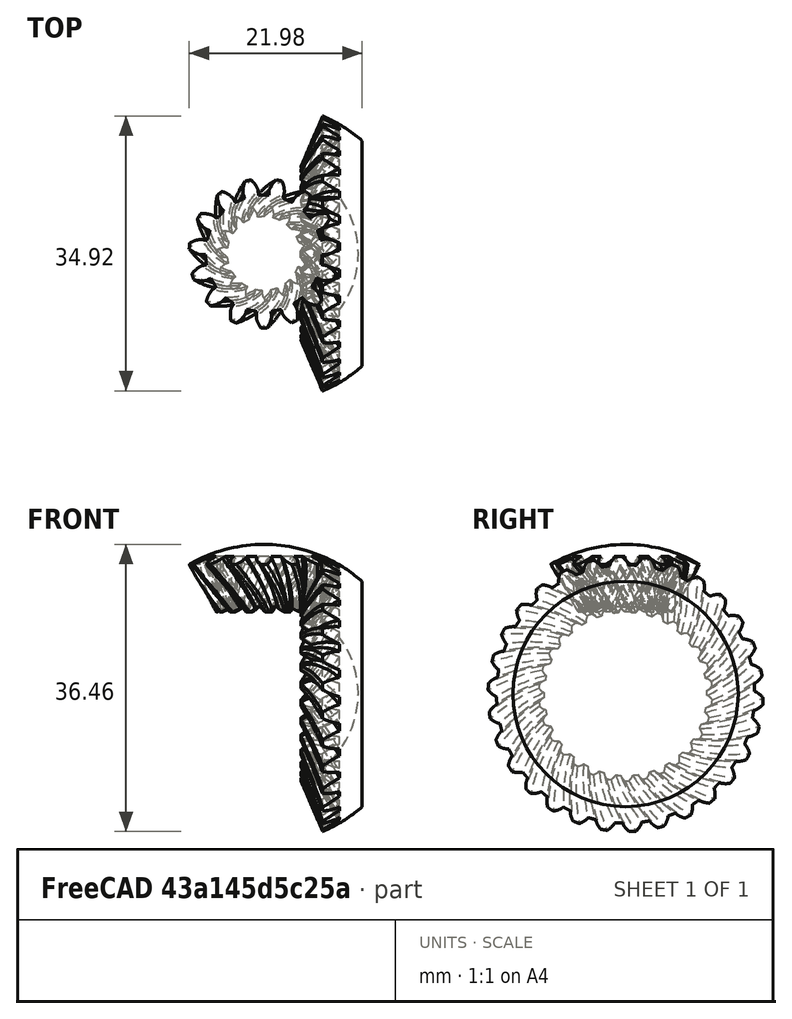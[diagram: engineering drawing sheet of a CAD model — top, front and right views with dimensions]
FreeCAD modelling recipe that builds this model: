
FCSTD DOCUMENT  (FreeCAD 0.17R13387 (Git))
Label: bevel_gear_animation
License: All rights reserved
LicenseURL: http://en.wikipedia.org/wiki/All_rights_reserved
objects: Part::FeaturePython×2, Part::Sphere×2, Part::MultiCommon×2, Part::Cut×1
note: 7 computed .brp shape members not serialized (recipe doc carries the construction recipe); baked Part::Feature solids carry a one-line shape summary decoded from their .brp

FEATURE [Part::FeaturePython] BevelGear  # WARN: FeaturePython — macro-defined, semantics opaque (R4)
  Placement = pos=(0,0,0) rot=(0,0,1;0.10472rad)
  backlash = 0
  beta = 20
  clearance = 0.1
  height = 10
  m = 1
  numpoints = 6
  pitch_angle = 26.5651
  pressure_angle = 20
  teeth = 15
  expr: pitch_angle = atan(0.5)
FEATURE [Part::FeaturePython] BevelGear001  # WARN: FeaturePython — macro-defined, semantics opaque (R4)
  Placement = pos=(0,0,0) rot=(0,1,0;1.5708rad)
  backlash = 0
  beta = -20
  clearance = 0.1
  height = 10
  m = 1
  numpoints = 6
  pitch_angle = 63.4349
  pressure_angle = 20
  teeth = 30
  expr: pitch_angle = 90° - atan(0.5)
FEATURE [Part::Sphere] Sphere  label="Kugel"
  Angle1 = -90
  Angle2 = 90
  Angle3 = 360
  AttacherType = Attacher::AttachEngine3D
  Placement = pos=(0,0,0) rot=(0,0,1;1.5708rad)
  Radius = 12
FEATURE [Part::Sphere] Sphere001  label="Kugel001"
  Angle1 = -90
  Angle2 = 90
  Angle3 = 360
  AttacherType = Attacher::AttachEngine3D
  Placement = pos=(0,0,0) rot=(0,0,1;1.5708rad)
  Radius = 19
FEATURE [Part::Cut] Cut
  Base = -> Sphere001
  Tool = -> Sphere
FEATURE [Part::MultiCommon] Common
  Shapes = -> [Cut,BevelGear001]
FEATURE [Part::MultiCommon] Common001
  Shapes = -> [Cut,BevelGear]
